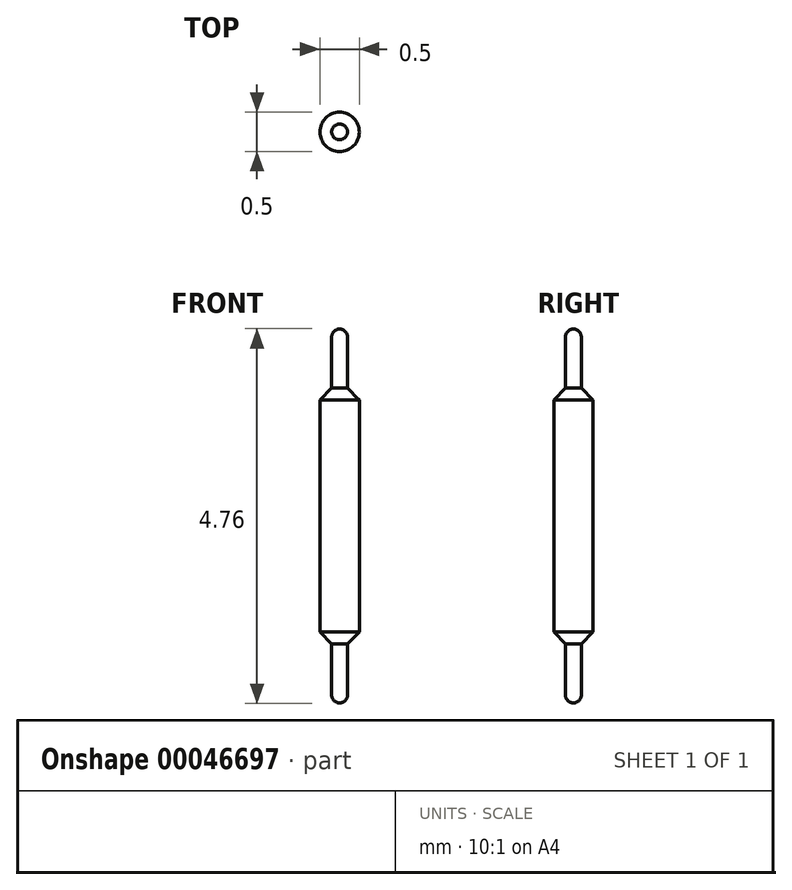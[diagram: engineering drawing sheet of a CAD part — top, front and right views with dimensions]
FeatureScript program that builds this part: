
annotation { "Feature Type Name" : "Feature", "Feature Type Description" : "" }
export const myFeature = defineFeature(function(context is Context, id is Id, definition is map)
    precondition{}
    {
        {
            var Q0;
            Q0=qCreatedBy(makeId("Right.planeOp"),FACE);
            var sketch = newSketch(context, id + "F0", { "sketchPlane" : qUnion([Q0])});
            skLineSegment(sketch, "E0", {"start": v(0, 0) * mm, "end": v(0, 1.48) * mm});
            skLineSegment(sketch, "E1", {"start": v(0, 0) * mm, "end": v(-0.25, 0) * mm});
            skLineSegment(sketch, "E2", {"start": v(-0.25, 0) * mm, "end": v(-0.25, 1.48) * mm});
            skLineSegment(sketch, "E3", {"start": v(-0.25, 1.48) * mm, "end": v(-0.25, 1.63) * mm});
            skLineSegment(sketch, "E4", {"start": v(-0.25, 1.63) * mm, "end": v(-0.15, 1.63) * mm});
            skLineSegment(sketch, "E5", {"start": v(-0.15, 1.63) * mm, "end": v(0, 1.48) * mm});
            skLineSegment(sketch, "E6", {"start": v(-0.15, 1.63) * mm, "end": v(-0.15, 2.27) * mm});
            skLineSegment(sketch, "E7", {"start": v(-0.25, 1.63) * mm, "end": v(-0.25, 2.38) * mm});
            skArc(sketch, "E8", {"start": v(-0.15, 2.27) * mm, "mid": v(-0.18, 2.35) * mm, "end": v(-0.25, 2.38) * mm});
            skLineSegment(sketch, "E9.MirrorCS", {"start": v(-0.25, -1.63) * mm, "end": v(-0.15, -1.63) * mm});
            skLineSegment(sketch, "E10.MirrorCS", {"start": v(-0.15, -1.63) * mm, "end": v(0, -1.48) * mm});
            skLineSegment(sketch, "E11.MirrorCS", {"start": v(0, 0) * mm, "end": v(0, -1.48) * mm});
            skLineSegment(sketch, "E12.MirrorCS", {"start": v(-0.15, -1.63) * mm, "end": v(-0.15, -2.27) * mm});
            skLineSegment(sketch, "E13.MirrorCS", {"start": v(-0.25, -1.63) * mm, "end": v(-0.25, -2.38) * mm});
            skArc(sketch, "E14.MirrorCS", {"start": v(-0.15, -2.27) * mm, "mid": v(-0.18, -2.35) * mm, "end": v(-0.25, -2.38) * mm});
            skLineSegment(sketch, "E15.MirrorCS", {"start": v(-0.25, 0) * mm, "end": v(-0.25, -1.48) * mm});
            skLineSegment(sketch, "E16.MirrorCS", {"start": v(-0.25, -1.48) * mm, "end": v(-0.25, -1.63) * mm});
            skSolve(sketch);
        }
        {
            var Q0;
            Q0=makeQuery(id+"F0.imprint","IMPRINT",FACE,{"disambiguationData":[TD([[makeQuery(id+"F0.imprint","IMPRINT",EDGE,{"derivedFrom":sQuery(id+"F0.wireOp",EDGE,"E4")}),1.0]])]});
            var Q1;
            Q1=makeQuery(id+"F0.imprint","IMPRINT",FACE,{"disambiguationData":[TD([[makeQuery(id+"F0.imprint","IMPRINT",EDGE,{"derivedFrom":sQuery(id+"F0.wireOp",EDGE,"E0")}),1.0]])]});
            var Q2;
            Q2=makeQuery(id+"F0.imprint","IMPRINT",FACE,{"disambiguationData":[TD([[makeQuery(id+"F0.imprint","IMPRINT",EDGE,{"derivedFrom":sQuery(id+"F0.wireOp",EDGE,"E1")}),1.0]])]});
            var Q3;
            Q3=makeQuery(id+"F0.imprint","IMPRINT",FACE,{"disambiguationData":[TD([[makeQuery(id+"F0.imprint","IMPRINT",EDGE,{"derivedFrom":sQuery(id+"F0.wireOp",EDGE,"E9.MirrorCS")}),-1.0]])]});
            var Q4;
            Q4=sQuery(id+"F0.wireOp",EDGE,"E15.MirrorCS");
            revolve(context, id + "F1", {"entities" : qUnion([Q0, Q1, Q2, Q3]), "axis" : qUnion([Q4]), "revolveType" : RevolveType.FULL});
        }
    });
